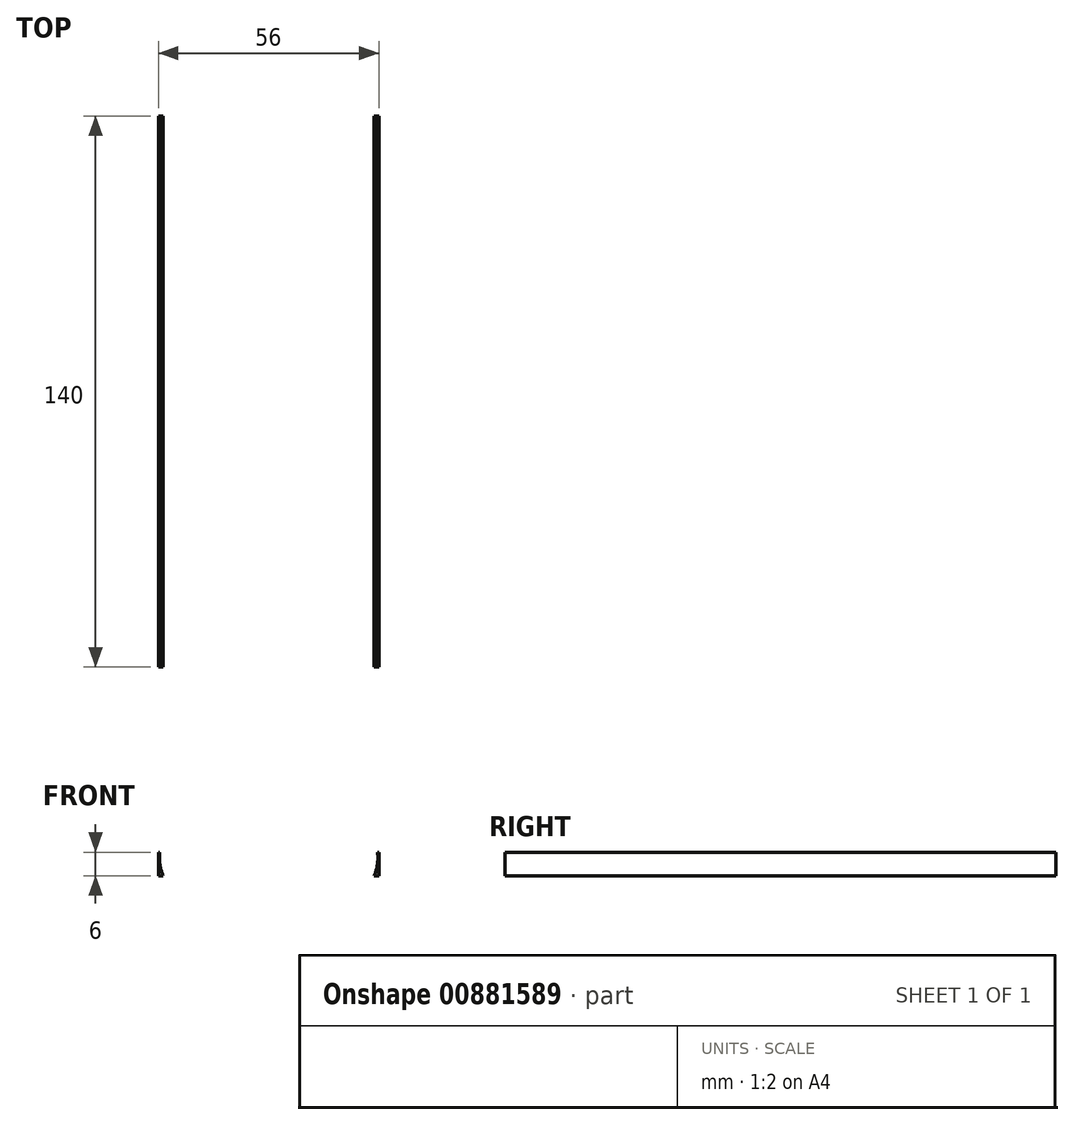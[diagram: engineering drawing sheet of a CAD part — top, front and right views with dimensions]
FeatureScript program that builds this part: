
annotation { "Feature Type Name" : "Feature", "Feature Type Description" : "" }
export const myFeature = defineFeature(function(context is Context, id is Id, definition is map)
    precondition{}
    {
        {
            var Q0;
            Q0=qCreatedBy(makeId("Top.planeOp"),FACE);
            var sketch = newSketch(context, id + "F0", { "sketchPlane" : qUnion([Q0])});
            skLineSegment(sketch, "E0.bottom", {"start": v(-56, 40.81) * mm, "end": v(0, 40.81) * mm});
            skLineSegment(sketch, "E0.top", {"start": v(-56, -99.19) * mm, "end": v(0, -99.19) * mm});
            skLineSegment(sketch, "E0.left", {"start": v(-56, 40.81) * mm, "end": v(-56, -99.19) * mm});
            skLineSegment(sketch, "E0.right", {"start": v(0, 40.81) * mm, "end": v(0, -99.19) * mm});
            skCircle(sketch, "E1", {"center": v(-28, 10.81) * mm, "radius": 20 * mm});
            skLineSegment(sketch, "E2.bottom", {"start": v(-15.5, -84.8) * mm, "end": v(-40.5, -84.8) * mm});
            skLineSegment(sketch, "E2.top", {"start": v(-15.5, -4.8) * mm, "end": v(-40.5, -4.8) * mm});
            skLineSegment(sketch, "E2.left", {"start": v(-15.5, -84.8) * mm, "end": v(-15.5, -4.8) * mm});
            skLineSegment(sketch, "E2.right", {"start": v(-40.5, -84.8) * mm, "end": v(-40.5, -4.8) * mm});
            skLineSegment(sketch, "E3", {"start": v(-28, 40.81) * mm, "end": v(-28, 10.81) * mm, "construction": true});
            skLineSegment(sketch, "E4", {"start": v(-28, -4.8) * mm, "end": v(-28, 10.81) * mm, "construction": true});
            skSolve(sketch);
        }
        {
            var Q0;
            Q0=makeQuery(id+"F0.imprint","IMPRINT",FACE,{"disambiguationData":[TD([[makeQuery(id+"F0.imprint","IMPRINT",EDGE,{"derivedFrom":sQuery(id+"F0.wireOp",EDGE,"E0.bottom")}),-1.0]])]});
            extrude(context, id + "F1", {"entities" : qUnion([Q0]), "depth" : 4 * mm, "offsetDistance" : 25 * mm});
        }
        {
            var Q0;
            Q0=makeQuery(id+"F1.opExtrude","CAP_EDGE",EDGE,{"disambiguationData":[OSD([sQuery(id+"F0.wireOp",EDGE,"E1")])],"isStart":false});
            var Q1;
            Q1=makeQuery(id+"F1.opExtrude","CAP_EDGE",EDGE,{"disambiguationData":[OSD([sQuery(id+"F0.wireOp",EDGE,"E2.bottom")])],"isStart":false});
            var Q2;
            Q2=makeQuery(id+"F1.opExtrude","CAP_EDGE",EDGE,{"disambiguationData":[OSD([sQuery(id+"F0.wireOp",EDGE,"E2.left")])],"isStart":false});
            var Q3;
            Q3=makeQuery(id+"F1.opExtrude","CAP_EDGE",EDGE,{"disambiguationData":[OSD([sQuery(id+"F0.wireOp",EDGE,"E2.right")])],"isStart":false});
            fillet(context, id + "F2", {"entities" : qUnion([Q0, Q1, Q2, Q3]), "radius" : 1 * mm, "tangentPropagation" : true, "allowEdgeOverflow" : false});
        }
        {
            var Q0;
            Q0=makeQuery(id+"F1.opExtrude","CAP_FACE",FACE,{"disambiguationData":[OSD([sQuery(id+"F0.wireOp",EDGE,"E0.bottom"),sQuery(id+"F0.wireOp",EDGE,"E0.top"),sQuery(id+"F0.wireOp",EDGE,"E0.left"),sQuery(id+"F0.wireOp",EDGE,"E0.right"),sQuery(id+"F0.wireOp",EDGE,"E1"),sQuery(id+"F0.wireOp",EDGE,"E2.bottom"),sQuery(id+"F0.wireOp",EDGE,"E2.left"),sQuery(id+"F0.wireOp",EDGE,"E2.right")])],"isStart":true});
            var sketch = newSketch(context, id + "F3", { "sketchPlane" : qUnion([Q0])});
            skLineSegment(sketch, "E5.bottom", {"start": v(-56, 99.19) * mm, "end": v(0, 99.19) * mm});
            skLineSegment(sketch, "E5.top", {"start": v(-56, -40.81) * mm, "end": v(0, -40.81) * mm});
            skLineSegment(sketch, "E5.left", {"start": v(-56, 99.19) * mm, "end": v(-56, -40.81) * mm});
            skLineSegment(sketch, "E5.right", {"start": v(0, 99.19) * mm, "end": v(0, -40.81) * mm});
            skSolve(sketch);
        }
        {
            var Q0;
            Q0 = qSketchRegion(id + "F3", true);
            extrude(context, id + "F4", {"entities" : qUnion([Q0]), "operationType" : NewBodyOperationType.ADD, "depth" : 2 * mm, "offsetDistance" : 25 * mm});
        }
        {
            var Q0;
            Q0=makeQuery(id+"F4.boolean.opBoolean","MERGE",FACE,{"derivedFrom":[makeQuery(id+"F1.opExtrude","SWEPT_FACE",FACE,{"disambiguationData":[OSD([sQuery(id+"F0.wireOp",EDGE,"E0.top")])]}),makeQuery(id+"F4.opExtrude","SWEPT_FACE",FACE,{"disambiguationData":[OSD([sQuery(id+"F3.wireOp",EDGE,"E5.bottom")])]})]});
            var sketch = newSketch(context, id + "F5", { "sketchPlane" : qUnion([Q0])});
            skPoint(sketch, "E6.centerSnap0", {"position": v(-0.25, 2.56) * mm});
            skPoint(sketch, "E6.centerSnap1", {"position": v(-28, 4) * mm});
            skEllipse(sketch, "E7", {"center": v(-28, 2.56) * mm, "majorRadius": 27.75 * mm, "minorRadius": 17.5 * mm, "majorAxis": v(1, 0)});
            skFitSpline(sketch, "E8.0", {"points": [v(4.72, 1.3) * mm, v(4.77, 2.56) * mm, v(4.72, 3.82) * mm, v(4.52, 5.48) * mm, v(4.04, 7.52) * mm, v(3.1, 9.84) * mm, v(1.86, 12.02) * mm, v(0.34, 14.05) * mm, v(-1.44, 15.93) * mm, v(-3.11, 17.35) * mm, v(-4.56, 18.41) * mm, v(-5.7, 19.17) * mm, v(-6.89, 19.88) * mm, v(-8.52, 20.77) * mm, v(-10.65, 21.76) * mm, v(-13.32, 22.76) * mm, v(-16.1, 23.6) * mm, v(-18.98, 24.24) * mm, v(-21.93, 24.7) * mm, v(-24.44, 24.95) * mm, v(-26.47, 25.04) * mm, v(-28, 25.07) * mm, v(-29.53, 25.04) * mm, v(-31.56, 24.95) * mm, v(-34.07, 24.7) * mm, v(-37.02, 24.24) * mm, v(-39.9, 23.6) * mm, v(-42.68, 22.76) * mm, v(-45.35, 21.76) * mm, v(-47.48, 20.77) * mm, v(-49.11, 19.88) * mm, v(-50.3, 19.17) * mm, v(-51.44, 18.41) * mm, v(-52.89, 17.35) * mm, v(-54.56, 15.93) * mm, v(-56.34, 14.05) * mm, v(-57.86, 12.02) * mm, v(-59.1, 9.84) * mm, v(-60.04, 7.52) * mm, v(-60.52, 5.48) * mm, v(-60.72, 3.82) * mm, v(-60.77, 2.56) * mm, v(-60.72, 1.3) * mm, v(-60.52, -0.37) * mm, v(-60.04, -2.4) * mm, v(-59.1, -4.73) * mm, v(-57.86, -6.91) * mm, v(-56.34, -8.94) * mm, v(-54.56, -10.81) * mm, v(-52.89, -12.24) * mm, v(-51.44, -13.3) * mm, v(-50.3, -14.05) * mm, v(-49.11, -14.77) * mm, v(-47.48, -15.65) * mm, v(-45.35, -16.64) * mm, v(-42.68, -17.65) * mm, v(-39.9, -18.48) * mm, v(-37.02, -19.13) * mm, v(-34.07, -19.6) * mm, v(-31.56, -19.83) * mm, v(-29.53, -19.93) * mm, v(-28, -19.95) * mm, v(-26.47, -19.93) * mm, v(-24.44, -19.83) * mm, v(-21.93, -19.6) * mm, v(-18.98, -19.13) * mm, v(-16.1, -18.48) * mm, v(-13.32, -17.65) * mm, v(-10.65, -16.64) * mm, v(-8.52, -15.65) * mm, v(-6.89, -14.77) * mm, v(-5.7, -14.05) * mm, v(-4.56, -13.3) * mm, v(-3.11, -12.24) * mm, v(-1.44, -10.81) * mm, v(0.34, -8.94) * mm, v(1.86, -6.91) * mm, v(3.1, -4.73) * mm, v(4.04, -2.4) * mm, v(4.52, -0.37) * mm, v(4.72, 1.3) * mm, v(4.77, 2.56) * mm, v(4.72, 3.82) * mm, v(4.72, 1.3) * mm]});
            skSolve(sketch);
        }
        {
            var Q0;
            Q0 = qSketchRegion(id + "F5", true);
            extrude(context, id + "F6", {"entities" : qUnion([Q0]), "operationType" : NewBodyOperationType.REMOVE, "oppositeDirection" : true, "depth" : 140 * mm, "offsetDistance" : 25 * mm});
        }
    });
